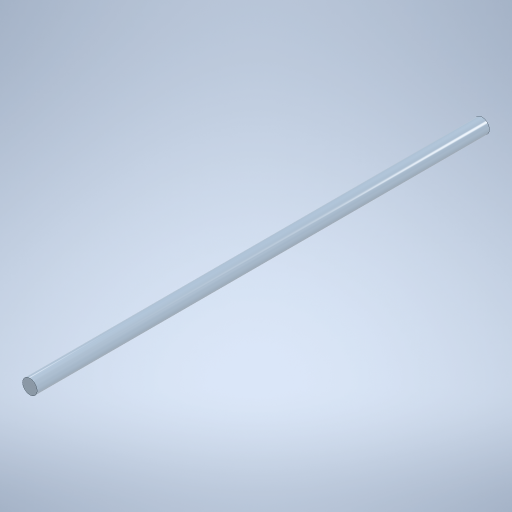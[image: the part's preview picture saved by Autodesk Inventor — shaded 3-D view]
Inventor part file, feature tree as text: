
AUTODESK INVENTOR PART (.ipt)
format: ipt  version: 2023.2 (Build 272271000, 271)  size: 241,664 bytes
history: native  units: mm
features: other x1, extrude x1, sketch x1
ambient origin geometry x8: Origin, YZ Plane, XZ Plane, XY Plane, X Axis, Y Axis, Z Axis, Center Point
bodies: Solid1 (feature_tree)
feature tree (3):
  other  "ACME Lead Screw 8mm"
  extrude  "Extrusion1"  Depth=250.0mm TaperAngle=0.0deg
  sketch  "Sketch1"  dims[d0=8.0mm d1=250.0mm d2=0.0mm]
